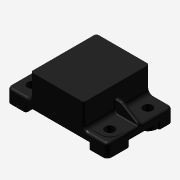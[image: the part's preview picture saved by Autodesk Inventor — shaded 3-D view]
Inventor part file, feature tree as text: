
AUTODESK INVENTOR PART (.ipt)
format: ipt  version: 2014 (Build 180170000, 170)  size: 484,352 bytes
history: native  units: mm (DEFAULTED — no unit token found)
features: sketch x12, extrude x11, fillet x5, mirror x3, plane x2, rib x1
ambient origin geometry x8: Origin, YZ Plane, XZ Plane, XY Plane, X Axis, Y Axis, Z Axis, Center Point
bodies: Solid1 (feature_tree)
feature tree (34):
  extrude  "Extrusion1"  Depth=5.08mm
  fillet  "Fillet19"  Radius=73.66mm
  extrude  "Extrusion4"  Depth=48.26mm TaperAngle=0.0deg
  fillet  "Fillet20"  Radius=3.048mm
  extrude  "Extrusion10"  Depth=1.524mm
  extrude  "Extrusion12"  Depth=10.16mm
  fillet  "Fillet21"  Radius=8.255mm
  plane  "Work Plane3"
  plane  "Work Plane4"
  mirror  "Mirror4"
  mirror  "Mirror5"
  extrude  "Extrusion11"  Depth=0.381mm TaperAngle=0.0deg
  extrude  "Extrusion13"  Depth=3.302mm
  extrude  "Extrusion14"  Depth=8.636mm
  extrude  "Extrusion15"  Depth=2.54mm
  extrude  "Extrusion16"  Depth=0.762mm
  extrude  "Extrusion5"  Depth=3.048mm
  extrude  "Extrusion6"  Depth=13.97mm
  rib  "Rib2"
  fillet  "Fillet22"  Radius=16.51mm
  fillet  "Fillet23"  Radius=4.826mm
  mirror  "Mirror6"
  sketch  "Sketch1"  dims[d1=23.099032mm d2=5.08mm d3=73.66mm]
  sketch  "Sketch5"  dims[d4=38.862mm d5=48.26mm d6=0.0mm d40=3.048mm]
  sketch  "Sketch6"  dims[d41=3.048mm d42=1.524mm]
  sketch  "Sketch7"  dims[d43=6.858mm d44=10.16mm d45=8.255mm]
  sketch  "Sketch8"  dims[d46=8.89mm d47=0.0mm d48=0.381mm d49=0.0mm]
  sketch  "Sketch14"  dims[d50=0.381mm d51=0.0mm d52=3.302mm]
  sketch  "Sketch15"  dims[d53=3.302mm d54=8.636mm]
  sketch  "Sketch16"  dims[d55=3.302mm d56=2.54mm]
  sketch  "Sketch17"  dims[d57=2.54mm d58=0.762mm]
  sketch  "Sketch18"  dims[d59=0.762mm d83=3.048mm]
  sketch  "Sketch19"  dims[d84=1.524mm d85=13.97mm d86=16.51mm d87=4.826mm d88=0.0mm]
  sketch  "Sketch20"  dims[d89=1.27mm d90=4.826mm d91=0.0mm d92=3.048mm d93=1.524mm d94=16.51mm d95=13.97mm d96=4.826mm d97=0.0mm d98=1.27mm d99=4.826mm d100=0.0mm d101=13.97mm d102=13.97mm d103=3.048mm d104=1.524mm d105=1.016mm d106=3.048mm d107=1.524mm d108=1.016mm d109=13.97mm d110=4.826mm d111=0.0mm d112=1.27mm d113=1.27mm d114=0.381mm d116=0.381mm d117=13.97mm d118=4.826mm d119=0.0mm d120=1.27mm d121=0.381mm d122=0.381mm d124=13.97mm d125=4.826mm d126=0.0mm]
